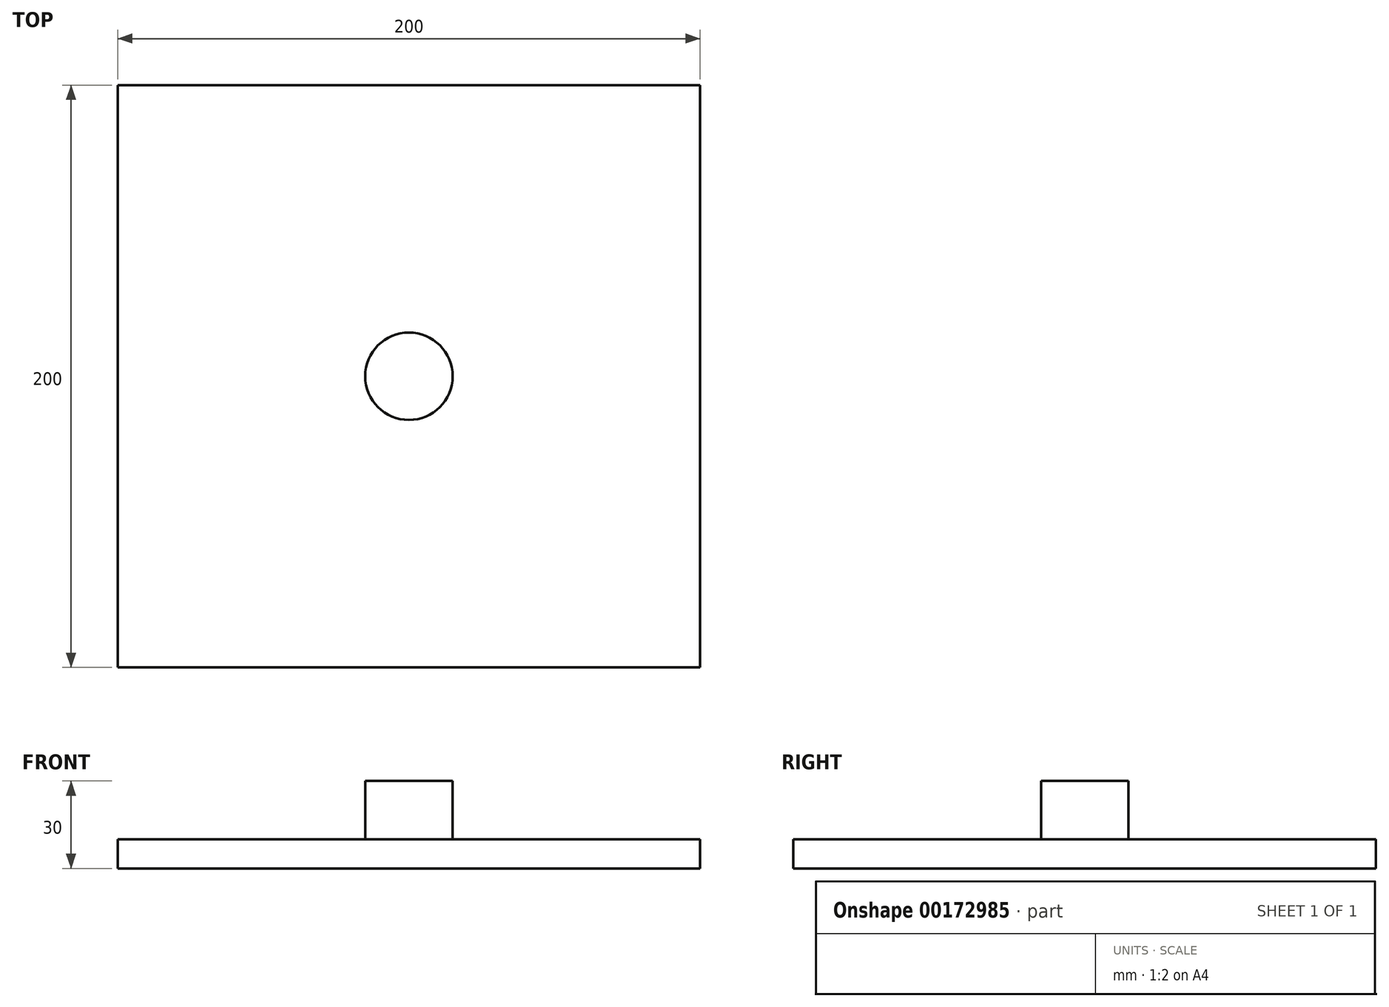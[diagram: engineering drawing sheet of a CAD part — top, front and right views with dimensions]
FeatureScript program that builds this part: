
annotation { "Feature Type Name" : "Feature", "Feature Type Description" : "" }
export const myFeature = defineFeature(function(context is Context, id is Id, definition is map)
    precondition{}
    {
        {
            var Q0;
            Q0=qCreatedBy(makeId("Top.planeOp"),FACE);
            var sketch = newSketch(context, id + "F0", { "sketchPlane" : qUnion([Q0])});
            skCircle(sketch, "E0", {"center": v(0, 0) * mm, "radius": 15 * mm});
            skSolve(sketch);
        }
        {
            var Q0;
            Q0 = qSketchRegion(id + "F0", true);
            extrude(context, id + "F1", {"entities" : qUnion([Q0]), "depth" : 20 * mm});
        }
        {
            var Q0;
            Q0=qCreatedBy(makeId("Top.planeOp"),FACE);
            var sketch = newSketch(context, id + "F2", { "sketchPlane" : qUnion([Q0])});
            skLineSegment(sketch, "E1.bottom", {"start": v(-100, -100) * mm, "end": v(100, -100) * mm});
            skLineSegment(sketch, "E1.top", {"start": v(-100, 100) * mm, "end": v(100, 100) * mm});
            skLineSegment(sketch, "E1.left", {"start": v(-100, -100) * mm, "end": v(-100, 100) * mm});
            skLineSegment(sketch, "E1.right", {"start": v(100, -100) * mm, "end": v(100, 100) * mm});
            skSolve(sketch);
        }
        {
            var Q0;
            Q0 = qSketchRegion(id + "F2", true);
            extrude(context, id + "F3", {"entities" : qUnion([Q0]), "operationType" : NewBodyOperationType.ADD, "oppositeDirection" : true, "depth" : 10 * mm});
        }
    });
